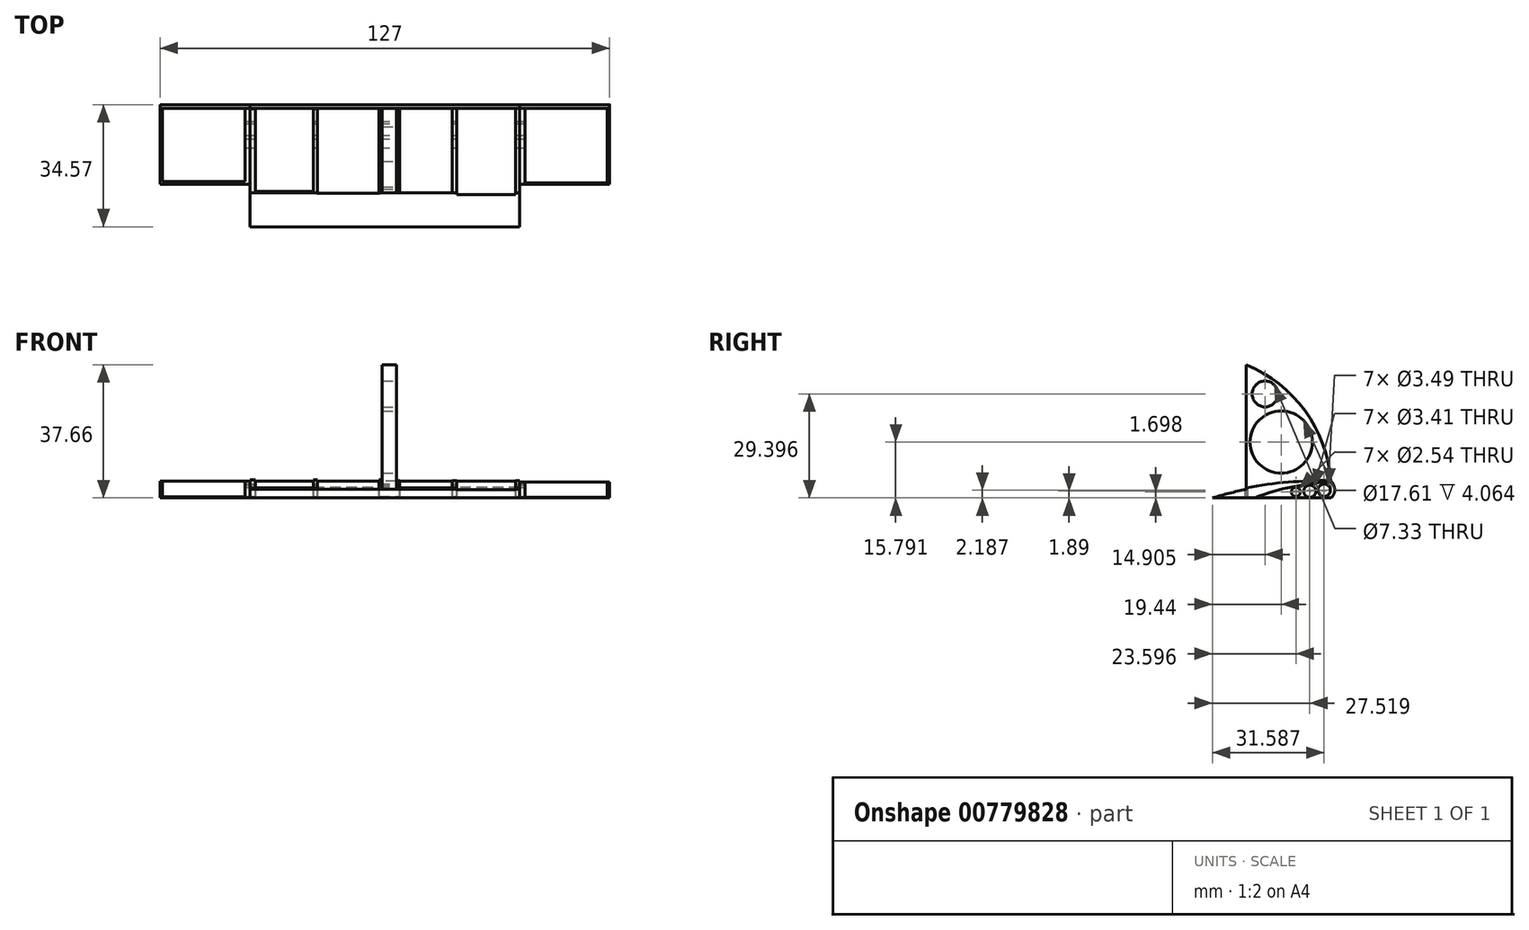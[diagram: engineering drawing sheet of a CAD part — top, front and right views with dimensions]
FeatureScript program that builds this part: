
annotation { "Feature Type Name" : "Feature", "Feature Type Description" : "" }
export const myFeature = defineFeature(function(context is Context, id is Id, definition is map)
    precondition{}
    {
        {
            var Q0;
            Q0=qCreatedBy(makeId("Right.planeOp"),FACE);
            var sketch = newSketch(context, id + "F0", { "sketchPlane" : qUnion([Q0])});
            skArc(sketch, "E0", {"start": v(0, 0) * mm, "mid": v(1.07, 2.39) * mm, "end": v(0, 4.78) * mm});
            skArc(sketch, "E1", {"start": v(0, 4.78) * mm, "mid": v(-16.9, 3.65) * mm, "end": v(-33.45, 0) * mm});
            skLineSegment(sketch, "E2", {"start": v(-33.45, 0) * mm, "end": v(0, 0) * mm});
            skSolve(sketch);
        }
        {
            var Q0;
            Q0 = qSketchRegion(id + "F0", true);
            extrude(context, id + "F1", {"entities" : qUnion([Q0]), "depth" : 76.2 * mm, "offsetDistance" : 25.4 * mm});
        }
        {
            var Q0;
            Q0=qCreatedBy(makeId("Right.planeOp"),FACE);
            var sketch = newSketch(context, id + "F2", { "sketchPlane" : qUnion([Q0])});
            skArc(sketch, "E3", {"start": v(0, 0) * mm, "mid": v(1.05, 2.36) * mm, "end": v(0, 4.72) * mm});
            skArc(sketch, "E4", {"start": v(0, 4.72) * mm, "mid": v(-10.88, 3.1) * mm, "end": v(-21.43, 0) * mm});
            skLineSegment(sketch, "E5", {"start": v(0, 0) * mm, "end": v(-21.43, 0) * mm});
            skSolve(sketch);
        }
        {
            var Q0;
            Q0 = qSketchRegion(id + "F2", true);
            extrude(context, id + "F3", {"entities" : qUnion([Q0]), "operationType" : NewBodyOperationType.ADD, "oppositeDirection" : true, "depth" : 25.4 * mm, "offsetDistance" : 25.4 * mm});
        }
        {
            var Q0;
            Q0=qCreatedBy(makeId("Right.planeOp"),FACE);
            var sketch = newSketch(context, id + "F4", { "sketchPlane" : qUnion([Q0])});
            skArc(sketch, "E6", {"start": v(0, 0) * mm, "mid": v(1.12, 2.23) * mm, "end": v(0, 4.45) * mm});
            skArc(sketch, "E7", {"start": v(0, 4.45) * mm, "mid": v(-10.92, 3.14) * mm, "end": v(-21.46, 0) * mm});
            skLineSegment(sketch, "E8", {"start": v(-21.46, 0) * mm, "end": v(0, 0) * mm});
            skSolve(sketch);
        }
        {
            var Q0;
            Q0 = qSketchRegion(id + "F4", true);
            extrude(context, id + "F5", {"entities" : qUnion([Q0]), "operationType" : NewBodyOperationType.ADD, "depth" : 101.6 * mm, "offsetDistance" : 25.4 * mm});
        }
        {
            var Q0;
            Q0=qCreatedBy(makeId("Right.planeOp"),FACE);
            var sketch = newSketch(context, id + "F6", { "sketchPlane" : qUnion([Q0])});
            skArc(sketch, "E9", {"start": v(0, 4.78) * mm, "mid": v(-7.26, 24.62) * mm, "end": v(-23.89, 37.66) * mm});
            skLineSegment(sketch, "E10", {"start": v(-23.89, 37.66) * mm, "end": v(-23.89, 1.38) * mm});
            skLineSegment(sketch, "E11", {"start": v(-23.89, 1.38) * mm, "end": v(0, 4.78) * mm});
            skSolve(sketch);
        }
        {
            var Q0;
            Q0 = qSketchRegion(id + "F6", true);
            extrude(context, id + "F7", {"entities" : qUnion([Q0]), "operationType" : NewBodyOperationType.ADD, "depth" : 76.2 * mm, "offsetDistance" : 25.4 * mm});
        }
        {
            var Q0;
            Q0=qCreatedBy(makeId("Right.planeOp"),FACE);
            cPlane(context, id + "F8", {"entities" : qUnion([Q0]), "cplaneType" : CPlaneType.OFFSET, "offset" : 78.74 * mm, "width" : 152.4 * mm, "height" : 152.4 * mm});
        }
        {
            var Q0;
            Q0=qCreatedBy(id+"F8.planeOp",FACE);
            var sketch = newSketch(context, id + "F9", { "sketchPlane" : qUnion([Q0])});
            skArc(sketch, "E12", {"start": v(0, 4.78) * mm, "mid": v(-17.65, 3.85) * mm, "end": v(-34.9, 0) * mm});
            skArc(sketch, "E13", {"start": v(-31.66, 52.88) * mm, "mid": v(-51.32, 27.55) * mm, "end": v(-34.9, 0) * mm});
            skArc(sketch, "E14", {"start": v(0, 4.78) * mm, "mid": v(6.96, 43.83) * mm, "end": v(-31.66, 52.88) * mm});
            skSolve(sketch);
        }
        {
            var Q0;
            Q0 = qSketchRegion(id + "F9", true);
            extrude(context, id + "F10", {"entities" : qUnion([Q0]), "operationType" : NewBodyOperationType.REMOVE, "oppositeDirection" : true, "depth" : 37.34 * mm, "offsetDistance" : 25.4 * mm});
        }
        {
            var Q0;
            Q0=qCreatedBy(makeId("Right.planeOp"),FACE);
            var sketch = newSketch(context, id + "F11", { "sketchPlane" : qUnion([Q0])});
            skArc(sketch, "E15", {"start": v(0, 5.1) * mm, "mid": v(-17.4, 3.88) * mm, "end": v(-34.42, 0) * mm});
            skArc(sketch, "E16", {"start": v(0, 5.1) * mm, "mid": v(12.8, 34.08) * mm, "end": v(-9.8, 56.28) * mm});
            skArc(sketch, "E17", {"start": v(-9.8, 56.28) * mm, "mid": v(-55.4, 42.7) * mm, "end": v(-34.42, 0) * mm});
            skSolve(sketch);
        }
        {
            var Q0;
            Q0 = qSketchRegion(id + "F11", true);
            extrude(context, id + "F12", {"entities" : qUnion([Q0]), "operationType" : NewBodyOperationType.REMOVE, "depth" : 37.34 * mm, "offsetDistance" : 25.4 * mm});
        }
        {
            var Q0;
            Q0=qCreatedBy(id+"F8.planeOp",FACE);
            var sketch = newSketch(context, id + "F13", { "sketchPlane" : qUnion([Q0])});
            skCircle(sketch, "E18", {"center": v(-14, 15.8) * mm, "radius": 8.8 * mm});
            skSolve(sketch);
        }
        {
            var Q0;
            Q0 = qSketchRegion(id + "F13", true);
            extrude(context, id + "F14", {"entities" : qUnion([Q0]), "operationType" : NewBodyOperationType.REMOVE, "oppositeDirection" : true, "depth" : 101.6 * mm, "offsetDistance" : 25.4 * mm});
        }
        {
            var Q0;
            Q0=qCreatedBy(id+"F8.planeOp",FACE);
            var sketch = newSketch(context, id + "F15", { "sketchPlane" : qUnion([Q0])});
            skCircle(sketch, "E19", {"center": v(-18.54, 29.4) * mm, "radius": 3.66 * mm});
            skSolve(sketch);
        }
        {
            var Q0;
            Q0 = qSketchRegion(id + "F15", true);
            extrude(context, id + "F16", {"entities" : qUnion([Q0]), "operationType" : NewBodyOperationType.REMOVE, "oppositeDirection" : true, "depth" : 116.84 * mm, "offsetDistance" : 25.4 * mm});
        }
        {
            var Q0;
            Q0=qCreatedBy(makeId("Right.planeOp"),FACE);
            cPlane(context, id + "F17", {"entities" : qUnion([Q0]), "cplaneType" : CPlaneType.OFFSET, "offset" : 159.26 * mm, "width" : 152.4 * mm, "height" : 152.4 * mm});
        }
        {
            var Q0;
            Q0=qCreatedBy(id+"F17.planeOp",FACE);
            var sketch = newSketch(context, id + "F18", { "sketchPlane" : qUnion([Q0])});
            skCircle(sketch, "E20", {"center": v(-1.86, 2.19) * mm, "radius": 1.74 * mm});
            skSolve(sketch);
        }
        {
            var Q0;
            Q0 = qSketchRegion(id + "F18", true);
            extrude(context, id + "F19", {"entities" : qUnion([Q0]), "operationType" : NewBodyOperationType.REMOVE, "oppositeDirection" : true, "depth" : 225.3 * mm, "offsetDistance" : 25.4 * mm});
        }
        {
            var Q0;
            Q0=qCreatedBy(id+"F17.planeOp",FACE);
            var sketch = newSketch(context, id + "F20", { "sketchPlane" : qUnion([Q0])});
            skCircle(sketch, "E21", {"center": v(-5.93, 1.89) * mm, "radius": 1.7 * mm});
            skSolve(sketch);
        }
        {
            var Q0;
            Q0 = qSketchRegion(id + "F20", true);
            extrude(context, id + "F21", {"entities" : qUnion([Q0]), "operationType" : NewBodyOperationType.REMOVE, "oppositeDirection" : true, "depth" : 213.1 * mm, "offsetDistance" : 25.4 * mm});
        }
        {
            var Q0;
            Q0=qCreatedBy(id+"F17.planeOp",FACE);
            var sketch = newSketch(context, id + "F22", { "sketchPlane" : qUnion([Q0])});
            skCircle(sketch, "E22", {"center": v(-9.85, 1.7) * mm, "radius": 1.27 * mm});
            skSolve(sketch);
        }
        {
            var Q0;
            Q0 = qSketchRegion(id + "F22", true);
            extrude(context, id + "F23", {"entities" : qUnion([Q0]), "operationType" : NewBodyOperationType.REMOVE, "oppositeDirection" : true, "depth" : 254 * mm, "offsetDistance" : 25.4 * mm});
        }
        {
            var Q0;
            Q0=qCreatedBy(makeId("Top.planeOp"),FACE);
            cPlane(context, id + "F24", {"entities" : qUnion([Q0]), "cplaneType" : CPlaneType.OFFSET, "offset" : 90.93 * mm, "oppositeDirection" : true, "width" : 152.4 * mm, "height" : 152.4 * mm});
        }
        {
            var Q0;
            Q0=qCreatedBy(id+"F24.planeOp",FACE);
            var sketch = newSketch(context, id + "F25", { "sketchPlane" : qUnion([Q0])});
            skLineSegment(sketch, "E23.bottom", {"start": v(-24.81, 0) * mm, "end": v(-1.4, 0) * mm});
            skLineSegment(sketch, "E23.top", {"start": v(-24.81, -20.68) * mm, "end": v(-1.4, -20.68) * mm});
            skLineSegment(sketch, "E23.left", {"start": v(-24.81, 0) * mm, "end": v(-24.81, -20.68) * mm});
            skLineSegment(sketch, "E23.right", {"start": v(-1.4, 0) * mm, "end": v(-1.4, -20.68) * mm});
            skSolve(sketch);
        }
        {
            var Q0;
            Q0 = qSketchRegion(id + "F25", true);
            extrude(context, id + "F26", {"entities" : qUnion([Q0]), "operationType" : NewBodyOperationType.REMOVE, "depth" : 209.8 * mm, "offsetDistance" : 25.4 * mm});
        }
        {
            var Q0;
            Q0=qCreatedBy(id+"F24.planeOp",FACE);
            var sketch = newSketch(context, id + "F27", { "sketchPlane" : qUnion([Q0])});
            skLineSegment(sketch, "E24.bottom", {"start": v(100.95, 0) * mm, "end": v(77.7, 0) * mm});
            skLineSegment(sketch, "E24.top", {"start": v(100.95, -21.01) * mm, "end": v(77.7, -21.01) * mm});
            skLineSegment(sketch, "E24.left", {"start": v(100.95, 0) * mm, "end": v(100.95, -21.01) * mm});
            skLineSegment(sketch, "E24.right", {"start": v(77.7, 0) * mm, "end": v(77.7, -21.01) * mm});
            skSolve(sketch);
        }
        {
            var Q0;
            Q0 = qSketchRegion(id + "F27", true);
            extrude(context, id + "F28", {"entities" : qUnion([Q0]), "operationType" : NewBodyOperationType.REMOVE, "depth" : 223.77 * mm, "offsetDistance" : 25.4 * mm});
        }
        {
            var Q0;
            Q0=qCreatedBy(id+"F24.planeOp",FACE);
            var sketch = newSketch(context, id + "F29", { "sketchPlane" : qUnion([Q0])});
            skLineSegment(sketch, "E25.bottom", {"start": v(75.07, 0) * mm, "end": v(58.42, 0) * mm});
            skLineSegment(sketch, "E25.top", {"start": v(75.07, -24.31) * mm, "end": v(58.42, -24.31) * mm});
            skLineSegment(sketch, "E25.left", {"start": v(75.07, 0) * mm, "end": v(75.07, -24.31) * mm});
            skLineSegment(sketch, "E25.right", {"start": v(58.42, 0) * mm, "end": v(58.42, -24.31) * mm});
            skSolve(sketch);
        }
        {
            var Q0;
            Q0 = qSketchRegion(id + "F29", true);
            extrude(context, id + "F30", {"entities" : qUnion([Q0]), "operationType" : NewBodyOperationType.REMOVE, "depth" : 495.05 * mm, "offsetDistance" : 25.4 * mm});
        }
        {
            var Q0;
            Q0=qCreatedBy(id+"F24.planeOp",FACE);
            var sketch = newSketch(context, id + "F31", { "sketchPlane" : qUnion([Q0])});
            skLineSegment(sketch, "E26.bottom", {"start": v(1.56, 0) * mm, "end": v(17.88, 0) * mm});
            skLineSegment(sketch, "E26.top", {"start": v(1.56, -23.49) * mm, "end": v(17.88, -23.49) * mm});
            skLineSegment(sketch, "E26.left", {"start": v(1.56, 0) * mm, "end": v(1.56, -23.49) * mm});
            skLineSegment(sketch, "E26.right", {"start": v(17.88, 0) * mm, "end": v(17.88, -23.49) * mm});
            skSolve(sketch);
        }
        {
            var Q0;
            Q0 = qSketchRegion(id + "F31", true);
            extrude(context, id + "F32", {"entities" : qUnion([Q0]), "operationType" : NewBodyOperationType.REMOVE, "depth" : 242.06 * mm, "offsetDistance" : 25.4 * mm});
        }
        {
            var Q0;
            Q0=qCreatedBy(id+"F24.planeOp",FACE);
            var sketch = newSketch(context, id + "F33", { "sketchPlane" : qUnion([Q0])});
            skLineSegment(sketch, "E27.bottom", {"start": v(36.5, 0) * mm, "end": v(19.03, 0) * mm});
            skLineSegment(sketch, "E27.top", {"start": v(36.5, -23.98) * mm, "end": v(19.03, -23.98) * mm});
            skLineSegment(sketch, "E27.left", {"start": v(36.5, 0) * mm, "end": v(36.5, -23.98) * mm});
            skLineSegment(sketch, "E27.right", {"start": v(19.03, 0) * mm, "end": v(19.03, -23.98) * mm});
            skSolve(sketch);
        }
        {
            var Q0;
            Q0 = qSketchRegion(id + "F33", true);
            extrude(context, id + "F34", {"entities" : qUnion([Q0]), "operationType" : NewBodyOperationType.REMOVE, "depth" : 243.84 * mm, "offsetDistance" : 25.4 * mm});
        }
        {
            var Q0;
            Q0=qCreatedBy(id+"F24.planeOp",FACE);
            var sketch = newSketch(context, id + "F35", { "sketchPlane" : qUnion([Q0])});
            skLineSegment(sketch, "E28.bottom", {"start": v(57.1, 0) * mm, "end": v(42.27, 0) * mm});
            skLineSegment(sketch, "E28.top", {"start": v(57.1, -23.82) * mm, "end": v(42.27, -23.82) * mm});
            skLineSegment(sketch, "E28.left", {"start": v(57.1, 0) * mm, "end": v(57.1, -23.82) * mm});
            skLineSegment(sketch, "E28.right", {"start": v(42.27, 0) * mm, "end": v(42.27, -23.82) * mm});
            skSolve(sketch);
        }
        {
            var Q0;
            Q0 = qSketchRegion(id + "F35", true);
            extrude(context, id + "F36", {"entities" : qUnion([Q0]), "operationType" : NewBodyOperationType.REMOVE, "depth" : 196.85 * mm, "offsetDistance" : 25.4 * mm});
        }
    });
